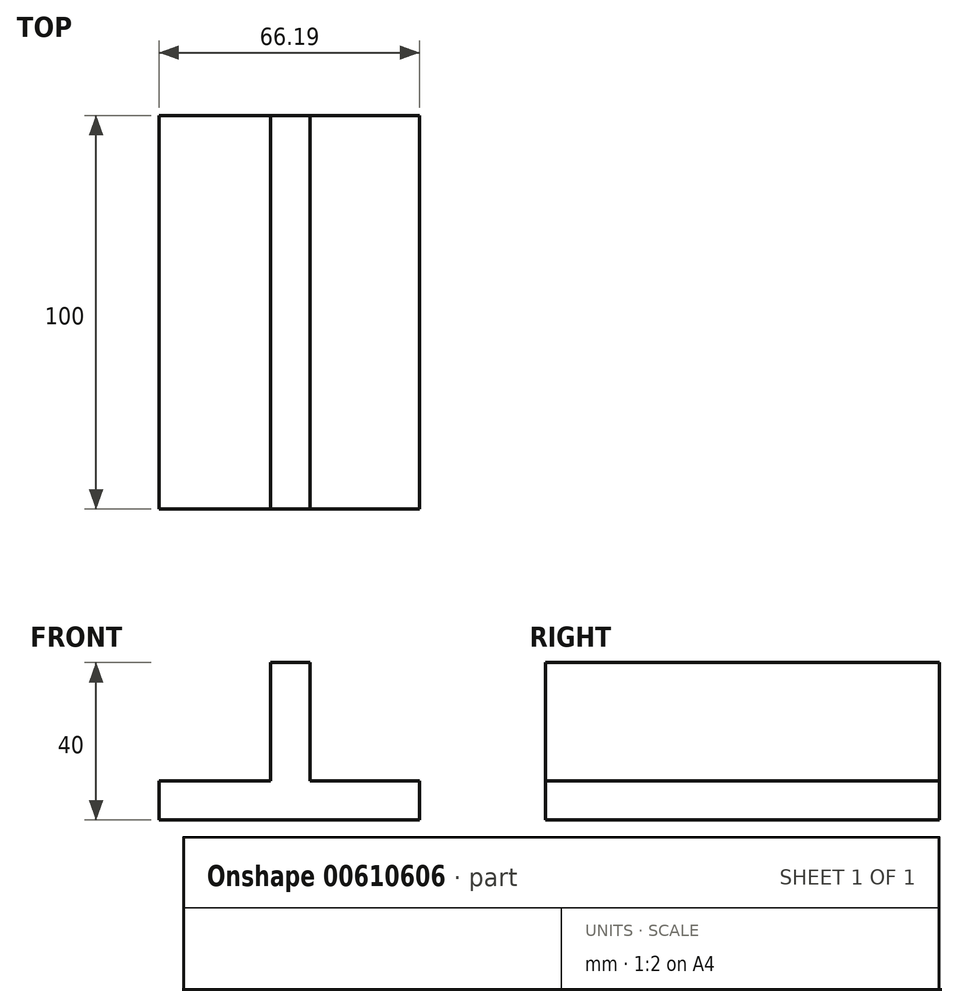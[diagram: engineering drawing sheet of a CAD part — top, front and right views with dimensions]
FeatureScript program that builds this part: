
annotation { "Feature Type Name" : "Feature", "Feature Type Description" : "" }
export const myFeature = defineFeature(function(context is Context, id is Id, definition is map)
    precondition{}
    {
        {
            var Q0;
            Q0=qCreatedBy(makeId("Front.planeOp"),FACE);
            var sketch = newSketch(context, id + "F0", { "sketchPlane" : qUnion([Q0])});
            skLineSegment(sketch, "E0", {"start": v(-5, 10) * mm, "end": v(-33.33, 10) * mm});
            skLineSegment(sketch, "E1", {"start": v(-33.33, 10) * mm, "end": v(-33.33, 0) * mm});
            skLineSegment(sketch, "E2", {"start": v(-33.33, 0) * mm, "end": v(32.86, 0) * mm});
            skLineSegment(sketch, "E3", {"start": v(32.86, 0) * mm, "end": v(32.86, 10) * mm});
            skLineSegment(sketch, "E4", {"start": v(32.86, 10) * mm, "end": v(5, 10) * mm});
            skLineSegment(sketch, "E5", {"start": v(5, 10) * mm, "end": v(5, 40) * mm});
            skLineSegment(sketch, "E6", {"start": v(5, 40) * mm, "end": v(-5, 40) * mm});
            skLineSegment(sketch, "E7", {"start": v(-5, 40) * mm, "end": v(-5, 10) * mm});
            skSolve(sketch);
        }
        {
            var Q0;
            Q0=makeQuery(id+"F0.imprint","IMPRINT",FACE,{"disambiguationData":[TD([[makeQuery(id+"F0.imprint","IMPRINT",EDGE,{"derivedFrom":sQuery(id+"F0.wireOp",EDGE,"E0")}),1.0]])]});
            extrude(context, id + "F1", {"entities" : qUnion([Q0]), "endBound" : BoundingType.SYMMETRIC, "depth" : 100 * mm, "offsetDistance" : 25 * mm});
        }
    });
